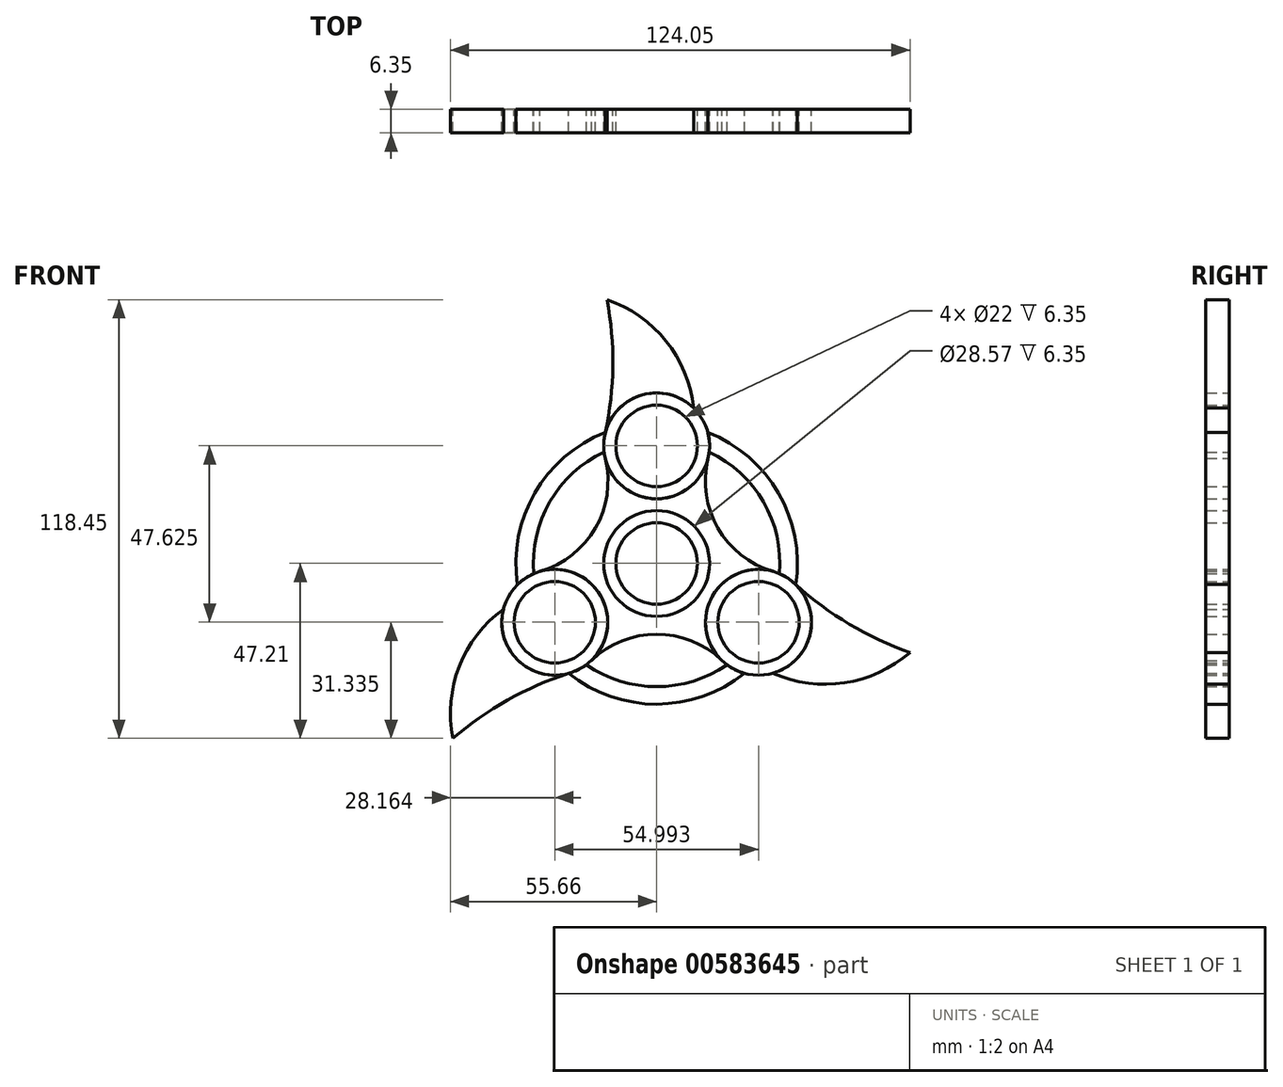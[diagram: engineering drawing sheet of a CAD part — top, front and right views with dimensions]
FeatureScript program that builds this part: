
annotation { "Feature Type Name" : "Feature", "Feature Type Description" : "" }
export const myFeature = defineFeature(function(context is Context, id is Id, definition is map)
    precondition{}
    {
        {
            var Q0;
            Q0=qCreatedBy(makeId("Front.planeOp"),FACE);
            var sketch = newSketch(context, id + "F0", { "sketchPlane" : qUnion([Q0])});
            skCircle(sketch, "E0", {"center": v(0, 0) * mm, "radius": 14.29 * mm});
            skCircle(sketch, "E1", {"center": v(0, 0) * mm, "radius": 11 * mm});
            skCircle(sketch, "E2", {"center": v(0, 31.75) * mm, "radius": 14.29 * mm});
            skCircle(sketch, "E3", {"center": v(0, 31.75) * mm, "radius": 11 * mm});
            skCircle(sketch, "E4.1.0", {"center": v(-27.5, -15.87) * mm, "radius": 14.29 * mm});
            skCircle(sketch, "E4.1.1", {"center": v(-27.5, -15.87) * mm, "radius": 11 * mm});
            skCircle(sketch, "E4.2.0", {"center": v(27.5, -15.88) * mm, "radius": 14.29 * mm});
            skCircle(sketch, "E4.2.1", {"center": v(27.5, -15.88) * mm, "radius": 11 * mm});
            skSolve(sketch);
        }
        {
            var Q0;
            Q0=qCreatedBy(makeId("Front.planeOp"),FACE);
            var sketch = newSketch(context, id + "F1", { "sketchPlane" : qUnion([Q0])});
            skCircle(sketch, "E5.0", {"center": v(0, 31.75) * mm, "radius": 14.29 * mm});
            skCircle(sketch, "E6.0.0", {"center": v(0, 31.75) * mm, "radius": 11 * mm});
            skCircle(sketch, "E7.0.0", {"center": v(0, 0) * mm, "radius": 11 * mm});
            skCircle(sketch, "E8.0", {"center": v(0, 0) * mm, "radius": 14.29 * mm});
            skCircle(sketch, "E9.0", {"center": v(-27.5, -15.87) * mm, "radius": 11 * mm});
            skCircle(sketch, "E10.0", {"center": v(-27.5, -15.87) * mm, "radius": 14.29 * mm});
            skCircle(sketch, "E11.0.0", {"center": v(27.5, -15.88) * mm, "radius": 11 * mm});
            skCircle(sketch, "E12.0", {"center": v(27.5, -15.88) * mm, "radius": 14.29 * mm});
            skArc(sketch, "E13", {"start": v(9.97, 41.99) * mm, "mid": v(2.56, 60.02) * mm, "end": v(-13.38, 71.24) * mm});
            skArc(sketch, "E14", {"start": v(-13.95, 34.82) * mm, "mid": v(-11.84, 53) * mm, "end": v(-13.38, 71.24) * mm});
            skArc(sketch, "E15.1.0", {"start": v(-41.35, -12.36) * mm, "mid": v(-53.25, -27.8) * mm, "end": v(-55, -47.2) * mm});
            skArc(sketch, "E15.1.1", {"start": v(-23.17, -29.5) * mm, "mid": v(-39.98, -36.75) * mm, "end": v(-55, -47.2) * mm});
            skArc(sketch, "E15.2.0", {"start": v(31.38, -29.62) * mm, "mid": v(50.7, -32.22) * mm, "end": v(68.39, -24.03) * mm});
            skArc(sketch, "E15.2.1", {"start": v(37.13, -5.32) * mm, "mid": v(51.82, -16.25) * mm, "end": v(68.39, -24.03) * mm});
            skPoint(sketch, "E16.start.orphan", {"position": v(-37.13, -5.32) * mm});
            skPoint(sketch, "E17.start.orphan", {"position": v(-34.53, -28.31) * mm});
            skArc(sketch, "E18", {"start": v(-23.73, -29.66) * mm, "mid": v(0, -37.98) * mm, "end": v(23.73, -29.66) * mm});
            skArc(sketch, "E19", {"start": v(-18.97, -27.34) * mm, "mid": v(0, -33.27) * mm, "end": v(18.97, -27.34) * mm});
            skArc(sketch, "E20.trimOffspring", {"start": v(37.55, -5.72) * mm, "mid": v(32.9, 19) * mm, "end": v(13.82, 35.38) * mm});
            skArc(sketch, "E21.trimOffspring", {"start": v(33.16, -2.76) * mm, "mid": v(28.81, 16.64) * mm, "end": v(14.2, 30.1) * mm});
            skArc(sketch, "E22.trimOffspring", {"start": v(-14.2, 30.1) * mm, "mid": v(-28.81, 16.64) * mm, "end": v(-33.16, -2.76) * mm});
            skArc(sketch, "E23.trimOffspring", {"start": v(-13.82, 35.38) * mm, "mid": v(-32.9, 19) * mm, "end": v(-37.55, -5.72) * mm});
            skArc(sketch, "E24", {"start": v(-33.17, -2.58) * mm, "mid": v(-16.54, 9.55) * mm, "end": v(-14.35, 30.02) * mm});
            skArc(sketch, "E25", {"start": v(14.35, 30.02) * mm, "mid": v(16.54, 9.55) * mm, "end": v(33.17, -2.58) * mm});
            skArc(sketch, "E26", {"start": v(18.82, -27.44) * mm, "mid": v(0, -19.1) * mm, "end": v(-18.82, -27.44) * mm});
            skSolve(sketch);
        }
        {
            var Q0;
            {var subQ0=sQuery(id+"F1.wireOp",EDGE,"E14");var subQ1=sQuery(id+"F1.wireOp",EDGE,"E5.0");var subQ2=makeQuery(id+"F1.imprint","INTERSECT",VERTEX,{"derivedFrom":[subQ1,subQ0]});Q0=makeQuery(id+"F1.imprint","IMPRINT",FACE,{"disambiguationData":[TD([[makeQuery(id+"F1.imprint","IMPRINT",EDGE,{"disambiguationData":[TD([[subQ2,-1.0]])],"derivedFrom":subQ1}),-1.0]])]});}
            var Q1;
            {var subQ0=sQuery(id+"F1.wireOp",EDGE,"E13");Q1=makeQuery(id+"F1.imprint","IMPRINT",FACE,{"disambiguationData":[TD([[makeQuery(id+"F1.imprint","IMPRINT",EDGE,{"derivedFrom":subQ0}),1.0]])]});}
            var Q2;
            Q2=makeQuery(id+"F0.imprint","IMPRINT",FACE,{"disambiguationData":[TD([[makeQuery(id+"F0.imprint","IMPRINT",EDGE,{"derivedFrom":sQuery(id+"F0.wireOp",EDGE,"E2")}),1.0]])]});
            var Q3;
            {var subQ3=sQuery(id+"F1.wireOp",EDGE,"E20.trimOffspring");var subQ6=sQuery(id+"F1.wireOp",EDGE,"E5.0");var subQ10=makeQuery(id+"F1.imprint","INTERSECT",VERTEX,{"derivedFrom":[subQ6,subQ3]});Q3=makeQuery(id+"F1.imprint","IMPRINT",FACE,{"disambiguationData":[TD([[makeQuery(id+"F1.imprint","IMPRINT",EDGE,{"disambiguationData":[TD([[subQ10,1.0]])],"derivedFrom":subQ6}),-1.0]])]});}
            var Q4;
            {var subQ3=sQuery(id+"F1.wireOp",EDGE,"E15.1.1");var subQ7=sQuery(id+"F1.wireOp",EDGE,"E10.0");var subQ8=makeQuery(id+"F1.imprint","INTERSECT",VERTEX,{"derivedFrom":[subQ7,subQ3]});Q4=makeQuery(id+"F1.imprint","IMPRINT",FACE,{"disambiguationData":[TD([[makeQuery(id+"F1.imprint","IMPRINT",EDGE,{"disambiguationData":[TD([[subQ8,-1.0]])],"derivedFrom":subQ7}),-1.0]])]});}
            var Q5;
            Q5=makeQuery(id+"F0.imprint","IMPRINT",FACE,{"disambiguationData":[TD([[makeQuery(id+"F0.imprint","IMPRINT",EDGE,{"derivedFrom":sQuery(id+"F0.wireOp",EDGE,"E4.2.0")}),1.0]])]});
            var Q6;
            {var subQ0=sQuery(id+"F1.wireOp",EDGE,"E15.2.0");Q6=makeQuery(id+"F1.imprint","IMPRINT",FACE,{"disambiguationData":[TD([[makeQuery(id+"F1.imprint","IMPRINT",EDGE,{"derivedFrom":subQ0}),1.0]])]});}
            var Q7;
            {var subQ0=sQuery(id+"F1.wireOp",EDGE,"E15.1.0");Q7=makeQuery(id+"F1.imprint","IMPRINT",FACE,{"disambiguationData":[TD([[makeQuery(id+"F1.imprint","IMPRINT",EDGE,{"derivedFrom":subQ0}),1.0]])]});}
            var Q8;
            Q8=makeQuery(id+"F0.imprint","IMPRINT",FACE,{"disambiguationData":[TD([[makeQuery(id+"F0.imprint","IMPRINT",EDGE,{"derivedFrom":sQuery(id+"F0.wireOp",EDGE,"E4.1.0")}),1.0]])]});
            var Q9;
            Q9=makeQuery(id+"F1.imprint","IMPRINT",FACE,{"disambiguationData":[TD([[makeQuery(id+"F1.imprint","IMPRINT",EDGE,{"derivedFrom":sQuery(id+"F1.wireOp",EDGE,"E8.0")}),-1.0]])]});
            var Q10;
            Q10=makeQuery(id+"F0.imprint","IMPRINT",FACE,{"disambiguationData":[TD([[makeQuery(id+"F0.imprint","IMPRINT",EDGE,{"derivedFrom":sQuery(id+"F0.wireOp",EDGE,"E0")}),1.0]])]});
            extrude(context, id + "F2", {"entities" : qUnion([Q0, Q1, Q2, Q3, Q4, Q5, Q6, Q7, Q8, Q9, Q10]), "depth" : 6.35 * mm, "offsetDistance" : 25.4 * mm});
        }
    });
